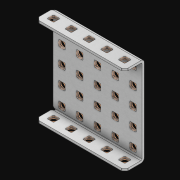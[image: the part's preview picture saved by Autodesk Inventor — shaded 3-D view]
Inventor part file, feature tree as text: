
AUTODESK INVENTOR PART (.ipt)
format: ipt  version: 2021 (Build 250183000, 183)  size: 2,895,872 bytes
history: native  units: in
note: dims shown in document units (in); Inventor stores cm internally (conversion verified against a paired STEP export)
features: extrude x36, other x35, sketch x4, thicken_offset x3, pattern_linear x3, imported_body x1
ambient origin geometry x8: Origin, YZ Plane, XZ Plane, XY Plane, X Axis, Y Axis, Z Axis, Center Point
bodies: Solid1 (feature_tree)
feature tree (82):
  thicken_offset  "Thicken1"
  thicken_offset  "Thicken2"
  thicken_offset  "Thicken3"
  pattern_linear  "Rectangular Pattern1"  Spacing1=0.001in  [1 undecoded]
  pattern_linear  "Rectangular Pattern2"  Spacing1=0.001in  [1 undecoded]
  pattern_linear  "Rectangular Pattern3"  Spacing1=0.182in  [1 undecoded]
  extrude  "Extrusion1"  Depth=0.063in TaperAngle=0.0deg
  sketch  "Sketch1"  dims[d0=0.001in]
  other  "Srf1"
  sketch  "Sketch2"  dims[d1=0.001in]
  other  "Srf2"
  sketch  "Sketch3"  dims[d2=0.001in]
  other  "Srf3"
  other  "Srf4"
  other  "Srf5"
  other  "Srf6"
  other  "Srf7"
  other  "Srf38"
  other  "Srf39"
  other  "Srf40"
  other  "Srf41"
  other  "Srf72"
  other  "Srf73"
  other  "Srf74"
  other  "Srf75"
  other  "Srf106"
  other  "Srf107"
  other  "Srf108"
  other  "Srf109"
  other  "Srf110"
  other  "Srf141"
  other  "Srf142"
  other  "Srf143"
  other  "Srf144"
  other  "Srf145"
  other  "Srf176"
  other  "Srf177"
  other  "Srf178"
  other  "Srf179"
  other  "Srf180"
  other  "Srf211"
  other  "Srf212"
  other  "Srf213"
  other  "Srf214"
  other  "Srf215"
  sketch  "Sketch4"  dims[d3=0.001in d4=0.001in d5=0.001in d6=0.182in d7=0.063in d8=0.0in d9=0.182in d10=0.063in d11=0.0in d12=0.182in d13=0.063in d14=0.0in d17=0.5in d18=1.9685in d20=0.5in d21=1.9685in d23=0.5in d24=1.9685in d26=0.5in d27=15.0in d28=0.0in]
  imported_body  "Imported1"
  extrude  "ExtrusionSrf1"  Depth=0.063in
  extrude  "ExtrusionSrf2"  Depth=0.063in TaperAngle=0.0deg
  extrude  "ExtrusionSrf3"  Depth=0.063in
  extrude  "ExtrusionSrf4"  Depth=0.063in TaperAngle=0.0deg
  extrude  "ExtrusionSrf5"  Depth=0.063in
  extrude  "ExtrusionSrf6"  Depth=0.063in
  extrude  "ExtrusionSrf7"  Depth=0.063in
  extrude  "ExtrusionSrf38"  Depth=0.063in
  extrude  "ExtrusionSrf39"  Depth=0.063in
  extrude  "ExtrusionSrf40"  Depth=0.063in
  extrude  "ExtrusionSrf41"  Depth=0.063in
  extrude  "ExtrusionSrf72"  TaperAngle=0.0deg  [1 undecoded]
  extrude  "ExtrusionSrf73"  [1 undecoded]
  extrude  "ExtrusionSrf74"  [1 undecoded]
  extrude  "ExtrusionSrf75"  [1 undecoded]
  extrude  "ExtrusionSrf106"  [1 undecoded]
  extrude  "ExtrusionSrf107"  [1 undecoded]
  extrude  "ExtrusionSrf108"  [1 undecoded]
  extrude  "ExtrusionSrf109"  [1 undecoded]
  extrude  "ExtrusionSrf110"  [1 undecoded]
  extrude  "ExtrusionSrf141"  [1 undecoded]
  extrude  "ExtrusionSrf142"  [1 undecoded]
  extrude  "ExtrusionSrf143"  [1 undecoded]
  extrude  "ExtrusionSrf144"  [1 undecoded]
  extrude  "ExtrusionSrf145"  [1 undecoded]
  extrude  "ExtrusionSrf176"  [1 undecoded]
  extrude  "ExtrusionSrf177"  [1 undecoded]
  extrude  "ExtrusionSrf178"  [1 undecoded]
  extrude  "ExtrusionSrf179"  [1 undecoded]
  extrude  "ExtrusionSrf180"  [1 undecoded]
  extrude  "ExtrusionSrf211"  [1 undecoded]
  extrude  "ExtrusionSrf212"  [1 undecoded]
  extrude  "ExtrusionSrf213"  [1 undecoded]
  extrude  "ExtrusionSrf214"  [1 undecoded]
  extrude  "ExtrusionSrf215"  [1 undecoded]
note: 27 required parameter values undecoded (feature->parameter linkage not recoverable at this tier; creation-order binding heuristic only, values carry confidence <= 0.55)
